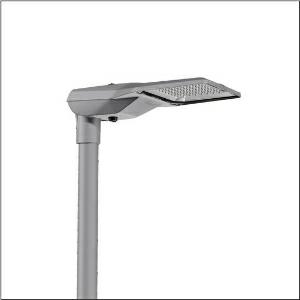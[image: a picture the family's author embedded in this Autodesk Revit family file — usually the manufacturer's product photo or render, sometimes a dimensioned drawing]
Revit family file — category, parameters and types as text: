
# Revit family: streetlight_sl_21_midi___st0_8a_5xe3c23t08lb_41e0
name_source: partatom
category: Lighting Fixtures
units: mm (PartAtom-declared; Revit-internal decimal feet)

## family parameters
Cut with Voids When Loaded = No
Host = Face
Light Source = No
Part Type = Normal
Room Calculation Point = No
Round Connector Dimension = Use Diameter
Shared = No

## types (1)
- --- (1 x LED, 11880 lm, 99.6 W, 2200K)
    Apparent Load = 100 VA
    CIE Flux Codes = 38 75 97 100 100
    Color Rendering = 70
    Color Temperature = 2200K
    Default Elevation = 1800 mm
    Description = Streetlight SL 21 midi, mast luminaire, primary light control with lens, of PMMA, primary optical cover: cover, of toughened safety glass, transparent, light distribution: ST0.8a, light emission: direct distribution, primary light characteristic: asymmetric, installation type: side-entry, post-top, LED, High Power LED, rated luminous flux: 11.880lm, luminous efficacy: 119lm/W, light colour: 722, colour temperature: 2200K, control gear: D4i, control: overheat protection, constant luminous flux control, time-dependent luminous flux control, flexible luminous flux parameterisation, pre-setting: logarithmic dimming characteristic, mains connection: 230..240V, AC, 50/60Hz, start of lifetime: 100W, end of service life: 102W, reduction: 45W, luminaire housing, of diecast aluminium, powder-coated, SITECO metallic grey (DB 702S), corrosivity category C5 high according to DIN EN ISO 12944, please order mast flange separately, inclination adjustable: 0°, 5°, 10°, 15°, sealing non-destructively replaceable, multi-level sealing system, length: 644mm, width: 335mm, height: 110mm, mast flange for spigot size: 42mm (side-entry): 5XC10008XM4, 60/48mm (side-entry/post-top): 5XC10108XM2, 76/60mm (side-entry/post-top): 5XC10108XM1, mounting height: 4..8m, Smart Interface below and above, protection rating (complete): IP66, insulation class (complete): insulation class II (safety insulation), certification: CE, ENEC, ENEC+, VDE, impact resistance: IK10, permissible operating ambient temperature for outdoor applications: -40..+50°C, standard-compliant lighting for roads and squares, packaging unit: 1 piece

Light Distribution: ST0.8a
    Height = 111 mm
    Lamp = 1 x LED
    Lamp Light Flux = 11880 lm
    Lamp Power = 99.6 W
    Lamp count = 1
    Length = 644 mm
    Luminous efficacy = 119 lm/W
    Manufacturer = Siteco
    ModVariant = No
    Model = 5XE3C23T08LB
    Number of Poles = 1
    OnlyDefault = Yes
    Power Factor = 1
    Product Name = Streetlight SL 21 midi | ST0.8a
    Product group = mast luminaire | pylon top
    ProductGroupID = 6100
    Protection Class = Protection class II
    Protection Degree = IP 66
    RLX_Detail_Level = 1
    RLX_Emergency_Light_Flux = 0 lm
    RLX_Emergency_Type = 0
    RLX_Emergency_Type_DB = No
    RlxData = <blob elided: 26989 chars, md5=9940983d>
    Socket = socket
    Standby Power = 0 W
    System Light Flux = 11880 lm
    System Power = 100 W
    Type Comments = factory setting: luminous flux: 100 % | dim-lin: 254 | 1020 mA
    Type Image = l_1004304.jpg
    URL = http://relux.com
    VarID = @adj_031007
    Voltage = 0 V
    Weight = 0.00 kg
    Width = 336 mm

## geometry (parser evidence)
native form markers: Blend x4, Sweep x11
no freeform markers — native parametric forms only
